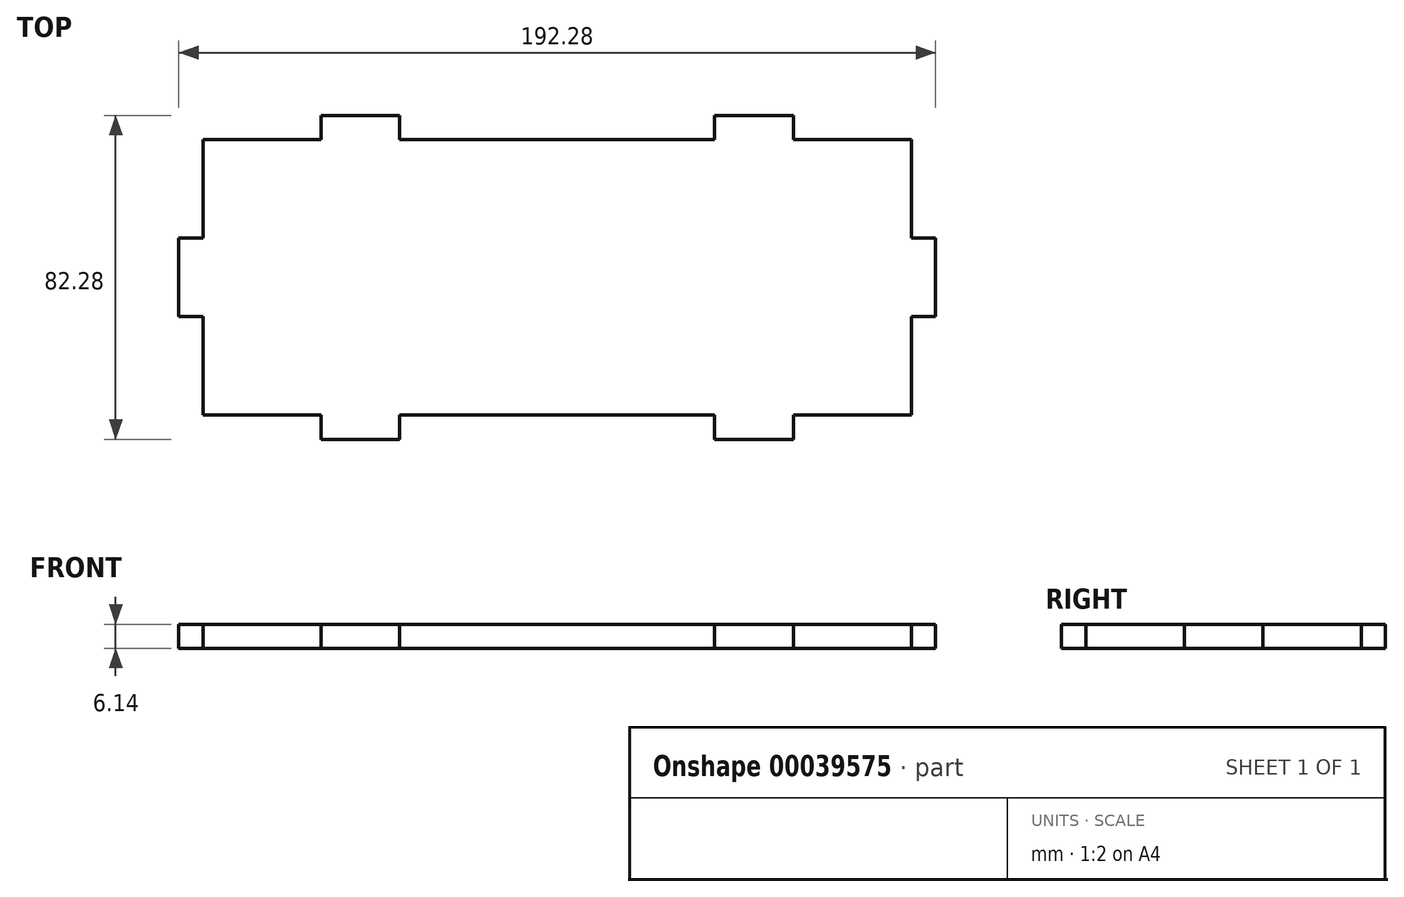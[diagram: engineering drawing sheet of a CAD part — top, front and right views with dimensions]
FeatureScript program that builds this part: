
annotation { "Feature Type Name" : "Feature", "Feature Type Description" : "" }
export const myFeature = defineFeature(function(context is Context, id is Id, definition is map)
    precondition{}
    {
        {
            assignVariable(context, id + "F0", {"name" : "PanelThickness", "anyValue" : 6.14});
        }
        {
            var Q0;
            Q0=qCreatedBy(makeId("Top.planeOp"),FACE);
            var sketch = newSketch(context, id + "F1", { "sketchPlane" : qUnion([Q0])});
            skLineSegment(sketch, "E0.rect.bottom", {"start": v(90, 35) * mm, "end": v(60, 35) * mm});
            skLineSegment(sketch, "E0.rect.top", {"start": v(90, -35) * mm, "end": v(60, -35) * mm});
            skLineSegment(sketch, "E0.rect.left", {"start": v(90, 35) * mm, "end": v(90, 10) * mm});
            skLineSegment(sketch, "E0.rect.right", {"start": v(-90, 35) * mm, "end": v(-90, 10) * mm});
            skLineSegment(sketch, "E1.top", {"start": v(40, -41.14) * mm, "end": v(60, -41.14) * mm});
            skLineSegment(sketch, "E1.left", {"start": v(40, -35) * mm, "end": v(40, -41.14) * mm});
            skLineSegment(sketch, "E1.right", {"start": v(60, -35) * mm, "end": v(60, -41.14) * mm});
            skLineSegment(sketch, "E2.MirrorCS", {"start": v(-40, -35) * mm, "end": v(-40, -41.14) * mm});
            skLineSegment(sketch, "E3.MirrorCS", {"start": v(-40, -41.14) * mm, "end": v(-60, -41.14) * mm});
            skLineSegment(sketch, "E4.MirrorCS", {"start": v(-60, -35) * mm, "end": v(-60, -41.14) * mm});
            skLineSegment(sketch, "E5.MirrorCS", {"start": v(-40, 41.14) * mm, "end": v(-60, 41.14) * mm});
            skLineSegment(sketch, "E6.MirrorCS", {"start": v(-40, 35) * mm, "end": v(-40, 41.14) * mm});
            skLineSegment(sketch, "E7.MirrorCS", {"start": v(-60, 35) * mm, "end": v(-60, 41.14) * mm});
            skLineSegment(sketch, "E8.MirrorCS", {"start": v(40, 35) * mm, "end": v(40, 41.14) * mm});
            skLineSegment(sketch, "E9.MirrorCS", {"start": v(40, 41.14) * mm, "end": v(60, 41.14) * mm});
            skLineSegment(sketch, "E10.MirrorCS", {"start": v(60, 35) * mm, "end": v(60, 41.14) * mm});
            skLineSegment(sketch, "E11.bottom", {"start": v(-90, -10) * mm, "end": v(-96.14, -10) * mm});
            skLineSegment(sketch, "E11.top", {"start": v(-90, 10) * mm, "end": v(-96.14, 10) * mm});
            skLineSegment(sketch, "E11.right", {"start": v(-96.14, -10) * mm, "end": v(-96.14, 10) * mm});
            skPoint(sketch, "E12", {"position": v(-96.14, 0) * mm});
            skLineSegment(sketch, "E13.MirrorCS", {"start": v(90, -10) * mm, "end": v(96.14, -10) * mm});
            skLineSegment(sketch, "E14.MirrorCS", {"start": v(96.14, -10) * mm, "end": v(96.14, 10) * mm});
            skLineSegment(sketch, "E15.MirrorCS", {"start": v(90, 10) * mm, "end": v(96.14, 10) * mm});
            skLineSegment(sketch, "E16.0", {"start": v(96.14, 41.14) * mm, "end": v(-96.14, 41.14) * mm, "construction": true});
            skLineSegment(sketch, "E17.0", {"start": v(-96.14, 41.14) * mm, "end": v(-96.14, -41.14) * mm, "construction": true});
            skLineSegment(sketch, "E18.0", {"start": v(96.14, 41.14) * mm, "end": v(96.14, -41.14) * mm, "construction": true});
            skLineSegment(sketch, "E19.0", {"start": v(96.14, -41.14) * mm, "end": v(-96.14, -41.14) * mm, "construction": true});
            skLineSegment(sketch, "E20", {"start": v(-60, 35) * mm, "end": v(-90, 35) * mm});
            skLineSegment(sketch, "E21", {"start": v(40, 35) * mm, "end": v(-40, 35) * mm});
            skLineSegment(sketch, "E22", {"start": v(90, -10) * mm, "end": v(90, -35) * mm});
            skLineSegment(sketch, "E23", {"start": v(40, -35) * mm, "end": v(-40, -35) * mm});
            skLineSegment(sketch, "E24", {"start": v(-60, -35) * mm, "end": v(-90, -35) * mm});
            skLineSegment(sketch, "E25", {"start": v(-90, -10) * mm, "end": v(-90, -35) * mm});
            skLineSegment(sketch, "E26", {"start": v(-200, 44.97) * mm, "end": v(-200, -58.1) * mm});
            skSolve(sketch);
        }
        {
            var Q0;
            {var subQ1=sQuery(id+"F1.wireOp",EDGE,"E1.bottom");Q0=makeQuery(id+"F1.imprint","IMPRINT",FACE,{"disambiguationData":[TD([[makeQuery(id+"F1.imprint","IMPRINT",EDGE,{"derivedFrom":subQ1}),1.0]])]});}
            var Q1;
            Q1=makeQuery(id+"F1.imprint","IMPRINT",FACE,{"disambiguationData":[TD([[makeQuery(id+"F1.imprint","IMPRINT",EDGE,{"derivedFrom":sQuery(id+"F1.wireOp",EDGE,"E11.bottom")}),-1.0]])]});
            var Q2;
            Q2=makeQuery(id+"F1.imprint","IMPRINT",FACE,{"disambiguationData":[TD([[makeQuery(id+"F1.imprint","IMPRINT",EDGE,{"derivedFrom":sQuery(id+"F1.wireOp",EDGE,"E5.MirrorCS")}),1.0]])]});
            var Q3;
            {var subQ1=sQuery(id+"F1.wireOp",EDGE,"E8.MirrorCS");Q3=makeQuery(id+"F1.imprint","IMPRINT",FACE,{"disambiguationData":[TD([[makeQuery(id+"F1.imprint","IMPRINT",EDGE,{"derivedFrom":subQ1}),-1.0]])]});}
            var Q4;
            {var subQ1=sQuery(id+"F1.wireOp",EDGE,"E13.MirrorCS");Q4=makeQuery(id+"F1.imprint","IMPRINT",FACE,{"disambiguationData":[TD([[makeQuery(id+"F1.imprint","IMPRINT",EDGE,{"derivedFrom":subQ1}),1.0]])]});}
            var Q5;
            Q5=makeQuery(id+"F1.imprint","IMPRINT",FACE,{"disambiguationData":[TD([[makeQuery(id+"F1.imprint","IMPRINT",EDGE,{"derivedFrom":sQuery(id+"F1.wireOp",EDGE,"E1.bottom")}),-1.0]])]});
            var Q6;
            {var subQ1=sQuery(id+"F1.wireOp",EDGE,"E2.MirrorCS");Q6=makeQuery(id+"F1.imprint","IMPRINT",FACE,{"disambiguationData":[TD([[makeQuery(id+"F1.imprint","IMPRINT",EDGE,{"derivedFrom":subQ1}),-1.0]])]});}
            extrude(context, id + "F2", {"entities" : qUnion([Q0, Q1, Q2, Q3, Q4, Q5, Q6]), "depth" : (getVariable(context, 'PanelThickness')) * mm});
        }
    });
